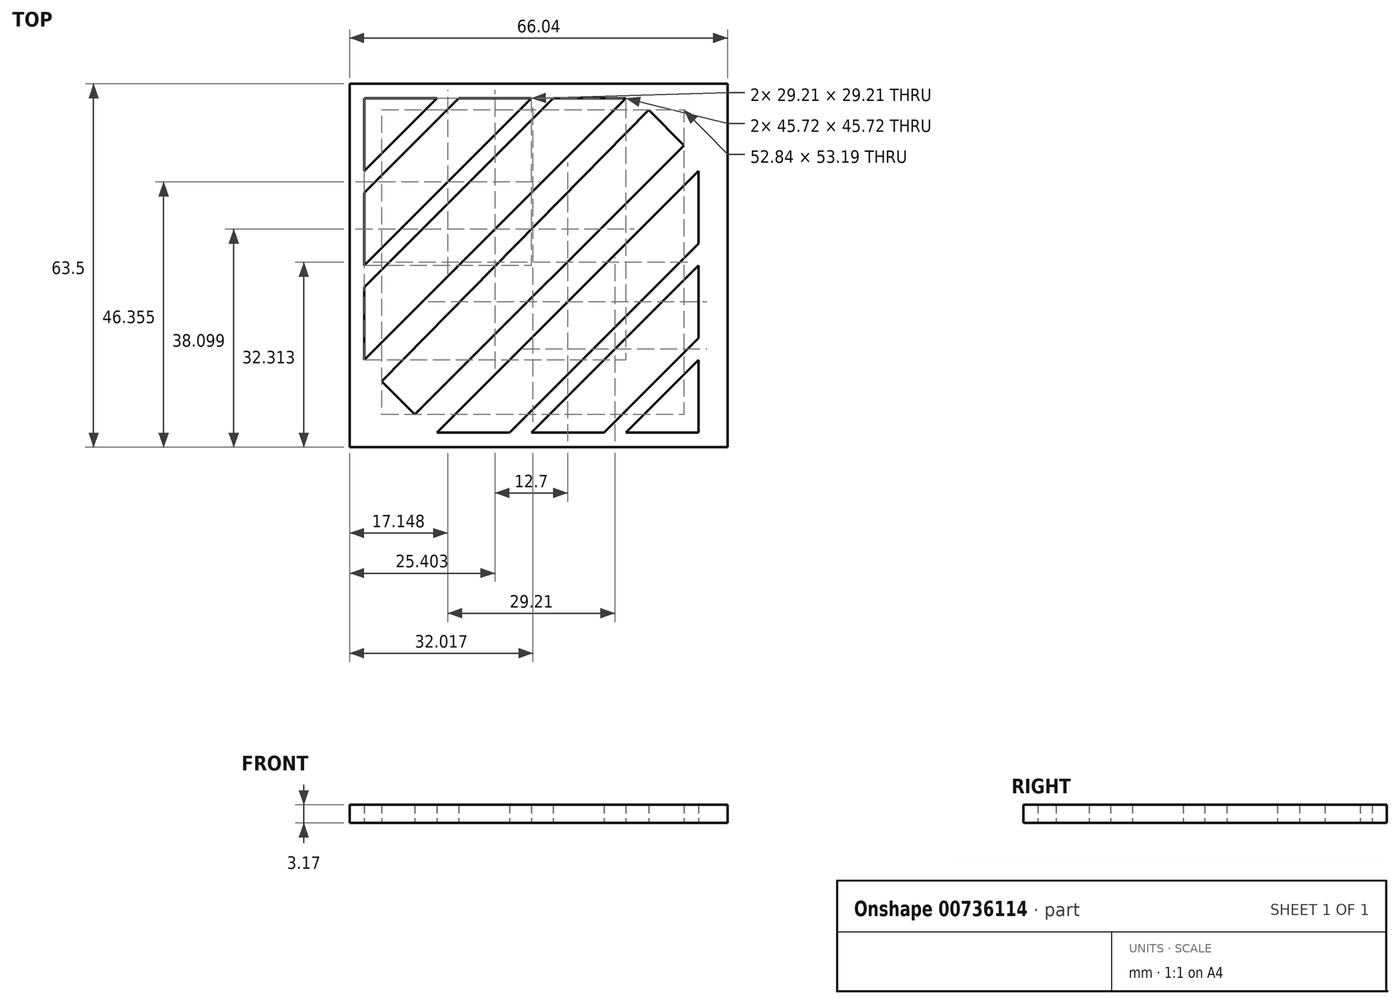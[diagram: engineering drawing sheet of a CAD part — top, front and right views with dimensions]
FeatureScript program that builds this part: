
annotation { "Feature Type Name" : "Feature", "Feature Type Description" : "" }
export const myFeature = defineFeature(function(context is Context, id is Id, definition is map)
    precondition{}
    {
        {
            var Q0;
            Q0=qCreatedBy(makeId("Top.planeOp"),FACE);
            var sketch = newSketch(context, id + "F0", { "sketchPlane" : qUnion([Q0])});
            skLineSegment(sketch, "E0.bottom", {"start": v(-34.47, 40.44) * mm, "end": v(31.57, 40.44) * mm});
            skLineSegment(sketch, "E0.top", {"start": v(-34.47, -23.06) * mm, "end": v(31.57, -23.06) * mm});
            skLineSegment(sketch, "E0.left", {"start": v(-34.47, 40.44) * mm, "end": v(-34.47, -23.06) * mm});
            skLineSegment(sketch, "E0.right", {"start": v(31.57, 40.44) * mm, "end": v(31.57, -23.06) * mm});
            skPoint(sketch, "E1", {"position": v(-31.93, 37.9) * mm});
            skPoint(sketch, "E2", {"position": v(-34.47, 37.9) * mm});
            skLineSegment(sketch, "E3", {"start": v(-31.93, 37.9) * mm, "end": v(-31.93, 25.2) * mm});
            skLineSegment(sketch, "E4", {"start": v(-31.93, 37.9) * mm, "end": v(-19.23, 37.9) * mm});
            skLineSegment(sketch, "E5", {"start": v(-31.93, 25.2) * mm, "end": v(-19.23, 37.9) * mm});
            skPoint(sketch, "E6", {"position": v(-15.42, 37.9) * mm});
            skPoint(sketch, "E7", {"position": v(-31.93, 21.39) * mm});
            skLineSegment(sketch, "E8", {"start": v(-31.93, 21.39) * mm, "end": v(-15.42, 37.9) * mm});
            skLineSegment(sketch, "E9", {"start": v(-15.42, 37.9) * mm, "end": v(-2.72, 37.9) * mm});
            skLineSegment(sketch, "E10", {"start": v(-31.93, 21.39) * mm, "end": v(-31.93, 8.69) * mm});
            skLineSegment(sketch, "E11", {"start": v(-31.93, 8.69) * mm, "end": v(-2.72, 37.9) * mm});
            skPoint(sketch, "E12", {"position": v(-31.93, 4.88) * mm});
            skPoint(sketch, "E13", {"position": v(1.1, 37.9) * mm});
            skLineSegment(sketch, "E14", {"start": v(1.1, 37.9) * mm, "end": v(13.8, 37.9) * mm});
            skLineSegment(sketch, "E15", {"start": v(-31.93, 4.88) * mm, "end": v(1.1, 37.9) * mm});
            skLineSegment(sketch, "E16", {"start": v(-31.93, 4.88) * mm, "end": v(-31.93, -7.82) * mm});
            skLineSegment(sketch, "E17", {"start": v(-31.93, -7.82) * mm, "end": v(13.8, 37.9) * mm});
            skLineSegment(sketch, "E18.MirrorCS", {"start": v(-19.23, -20.52) * mm, "end": v(26.5, 25.2) * mm});
            skLineSegment(sketch, "E19.MirrorCS", {"start": v(26.5, 12.5) * mm, "end": v(26.5, 25.2) * mm});
            skLineSegment(sketch, "E20.MirrorCS", {"start": v(-6.53, -20.52) * mm, "end": v(26.5, 12.5) * mm});
            skLineSegment(sketch, "E21.MirrorCS", {"start": v(-6.53, -20.52) * mm, "end": v(-19.23, -20.52) * mm});
            skLineSegment(sketch, "E22.MirrorCS", {"start": v(-2.72, -20.52) * mm, "end": v(26.5, 8.69) * mm});
            skLineSegment(sketch, "E23.MirrorCS", {"start": v(26.5, -4.01) * mm, "end": v(26.5, 8.69) * mm});
            skLineSegment(sketch, "E24.MirrorCS", {"start": v(9.98, -20.52) * mm, "end": v(26.5, -4.01) * mm});
            skLineSegment(sketch, "E25.MirrorCS", {"start": v(9.98, -20.52) * mm, "end": v(-2.72, -20.52) * mm});
            skLineSegment(sketch, "E26.MirrorCS", {"start": v(26.5, -20.52) * mm, "end": v(13.8, -20.52) * mm});
            skLineSegment(sketch, "E27.MirrorCS", {"start": v(26.5, -20.52) * mm, "end": v(26.5, -7.82) * mm});
            skLineSegment(sketch, "E28.MirrorCS", {"start": v(13.8, -20.52) * mm, "end": v(26.5, -7.82) * mm});
            skLineSegment(sketch, "E29", {"start": v(-28.87, -11.52) * mm, "end": v(-23.05, -17.34) * mm});
            skLineSegment(sketch, "E30", {"start": v(-23.05, -17.34) * mm, "end": v(23.97, 29.67) * mm});
            skLineSegment(sketch, "E31", {"start": v(23.97, 29.67) * mm, "end": v(17.79, 35.85) * mm});
            skLineSegment(sketch, "E32", {"start": v(17.79, 35.85) * mm, "end": v(-28.87, -11.52) * mm});
            skSolve(sketch);
        }
        {
            var Q0;
            Q0=makeQuery(id+"F0.imprint","IMPRINT",FACE,{"disambiguationData":[TD([[makeQuery(id+"F0.imprint","IMPRINT",EDGE,{"derivedFrom":sQuery(id+"F0.wireOp",EDGE,"E0.bottom")}),-1.0]])]});
            extrude(context, id + "F1", {"entities" : qUnion([Q0]), "depth" : 3.17 * mm, "offsetDistance" : 25.4 * mm});
        }
    });
